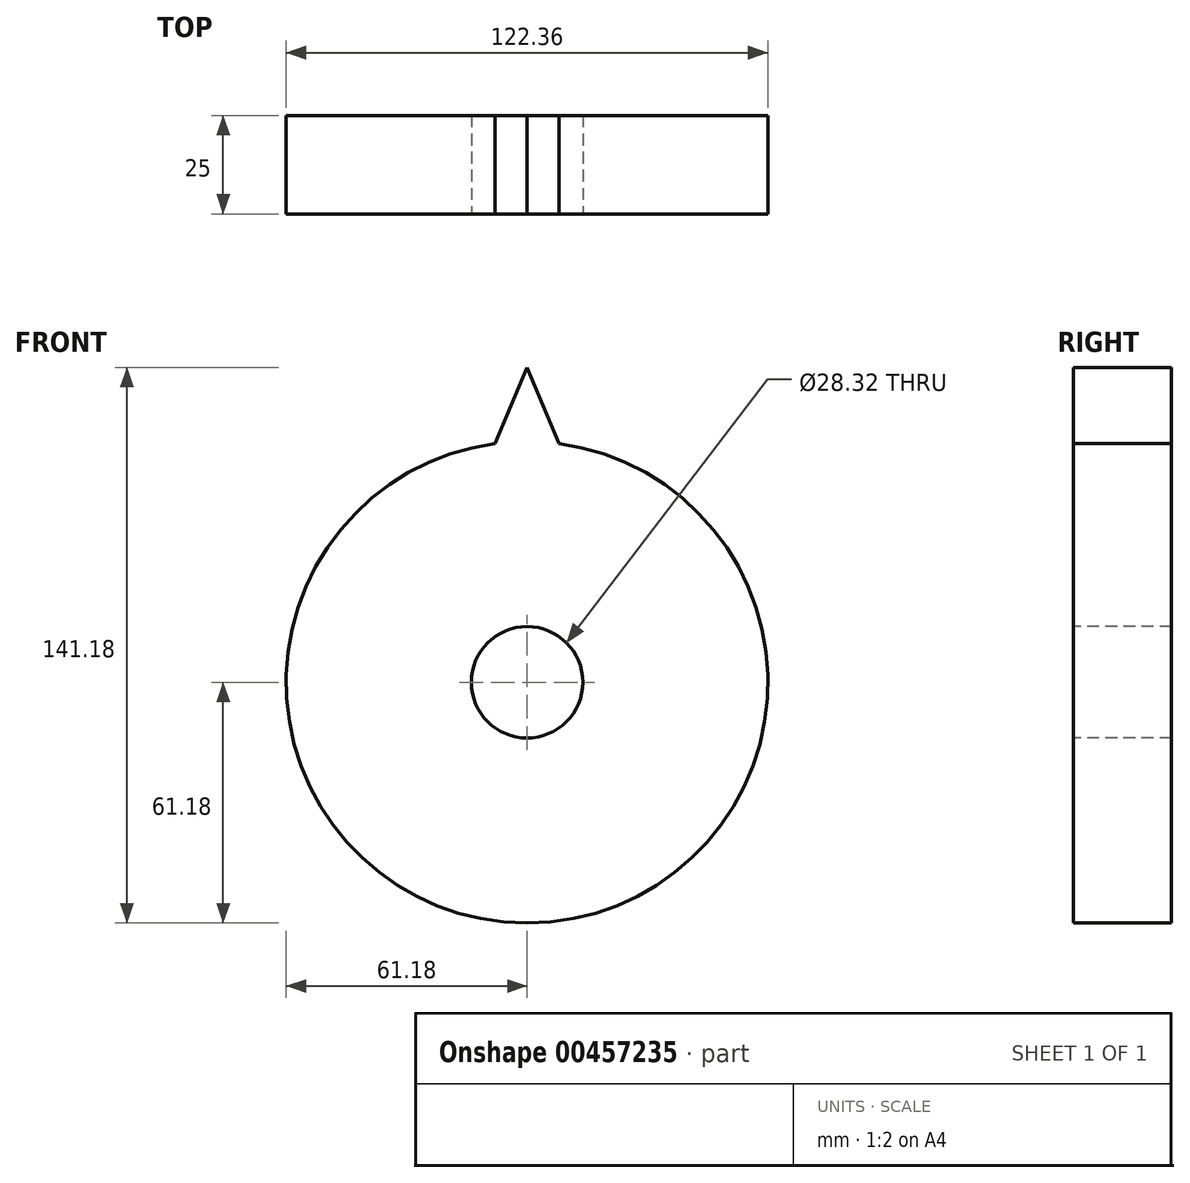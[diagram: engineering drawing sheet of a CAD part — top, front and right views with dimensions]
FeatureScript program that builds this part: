
annotation { "Feature Type Name" : "Feature", "Feature Type Description" : "" }
export const myFeature = defineFeature(function(context is Context, id is Id, definition is map)
    precondition{}
    {
        {
            var Q0;
            Q0=qCreatedBy(makeId("Front.planeOp"),FACE);
            var sketch = newSketch(context, id + "F0", { "sketchPlane" : qUnion([Q0])});
            skCircle(sketch, "E0", {"center": v(0, 0) * mm, "radius": 61.18 * mm});
            skSolve(sketch);
        }
        {
            var Q0;
            Q0=makeQuery(id+"F0.imprint","IMPRINT",FACE,{"disambiguationData":[TD([[makeQuery(id+"F0.imprint","IMPRINT",EDGE,{"derivedFrom":sQuery(id+"F0.wireOp",EDGE,"E0")}),1.0]])]});
            extrude(context, id + "F1", {"entities" : qUnion([Q0]), "depth" : 25 * mm});
        }
        {
            var Q0;
            Q0=makeQuery(id+"F1.opExtrude","CAP_FACE",FACE,{"disambiguationData":[OSD([sQuery(id+"F0.wireOp",EDGE,"E0")])],"isStart":false});
            var sketch = newSketch(context, id + "F2", { "sketchPlane" : qUnion([Q0])});
            skCircle(sketch, "E1", {"center": v(0, 0) * mm, "radius": 14.16 * mm});
            skSolve(sketch);
        }
        {
            var Q0;
            Q0 = qSketchRegion(id + "F2", true);
            extrude(context, id + "F3", {"entities" : qUnion([Q0]), "operationType" : NewBodyOperationType.REMOVE, "oppositeDirection" : true, "depth" : 25 * mm});
        }
        {
            var Q0;
            Q0=qCreatedBy(makeId("Front.planeOp"),FACE);
            var sketch = newSketch(context, id + "F4", { "sketchPlane" : qUnion([Q0])});
            skLineSegment(sketch, "E2", {"start": v(-8.14, 60.64) * mm, "end": v(0, 80) * mm});
            skLineSegment(sketch, "E3", {"start": v(0, 80) * mm, "end": v(8.14, 60.64) * mm});
            skCircle(sketch, "E4.2", {"center": v(0, 0) * mm, "radius": 61.18 * mm});
            skSolve(sketch);
        }
        {
            var Q0;
            {var subQ0=sQuery(id+"F4.wireOp",EDGE,"E2");Q0=makeQuery(id+"F4.imprint","IMPRINT",FACE,{"disambiguationData":[TD([[makeQuery(id+"F4.imprint","IMPRINT",EDGE,{"derivedFrom":subQ0}),-1.0]])]});}
            extrude(context, id + "F5", {"entities" : qUnion([Q0]), "operationType" : NewBodyOperationType.ADD, "depth" : 25 * mm});
        }
    });
